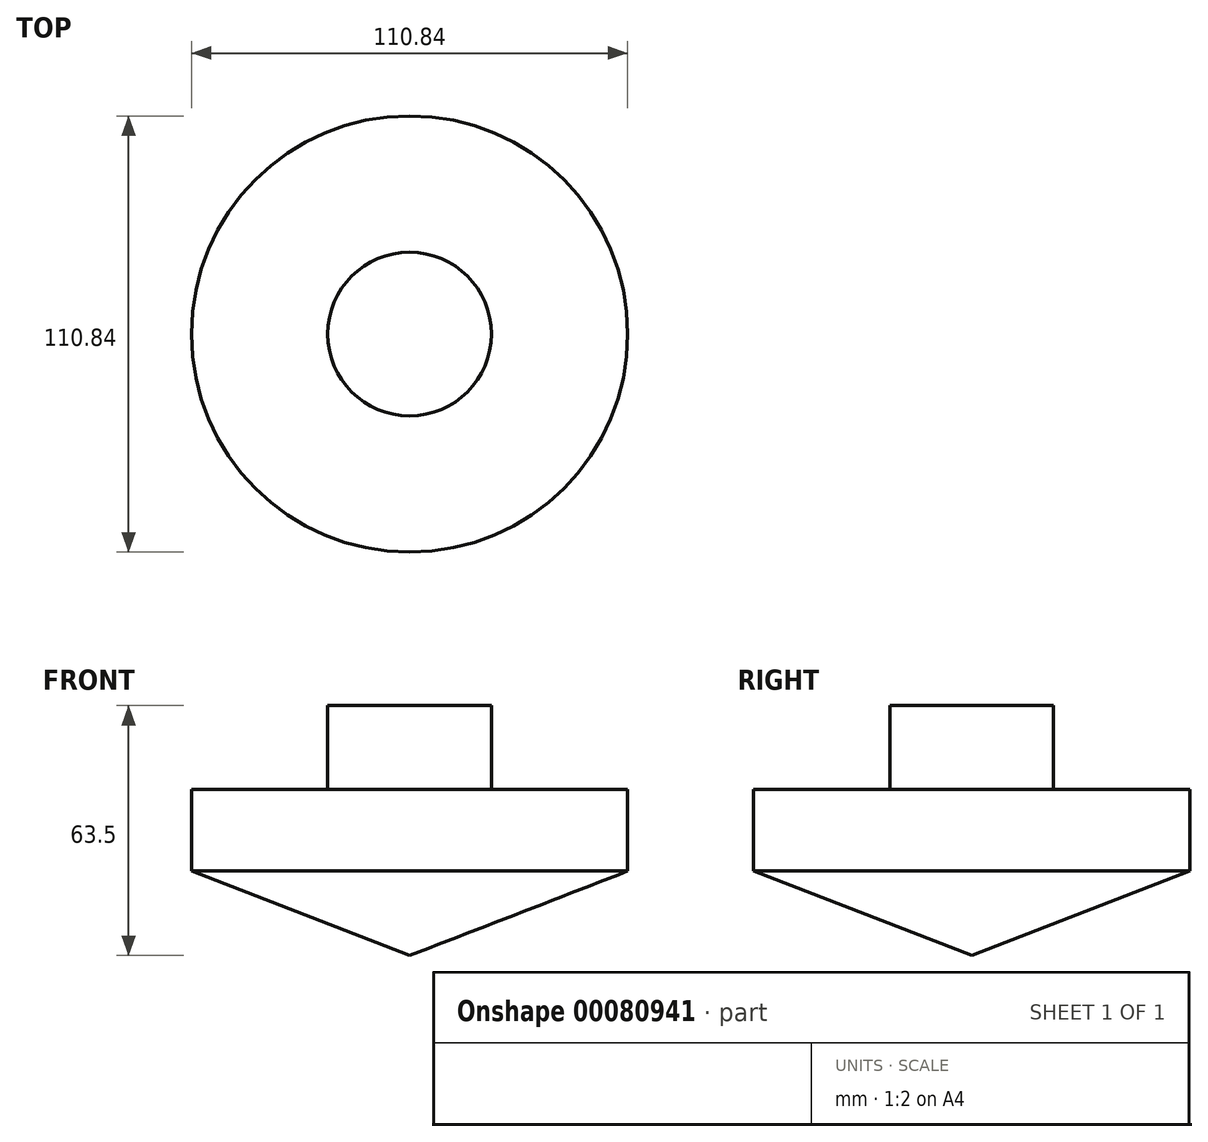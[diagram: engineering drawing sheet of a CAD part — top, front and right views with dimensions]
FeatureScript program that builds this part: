
annotation { "Feature Type Name" : "Feature", "Feature Type Description" : "" }
export const myFeature = defineFeature(function(context is Context, id is Id, definition is map)
    precondition{}
    {
        {
            var Q0;
            Q0=qCreatedBy(makeId("Front.planeOp"),FACE);
            var sketch = newSketch(context, id + "F0", { "sketchPlane" : qUnion([Q0])});
            skLineSegment(sketch, "E0", {"start": v(0, 0) * mm, "end": v(55.42, 21.47) * mm});
            skLineSegment(sketch, "E1", {"start": v(55.42, 21.47) * mm, "end": v(55.42, 42.26) * mm});
            skLineSegment(sketch, "E2", {"start": v(55.42, 42.26) * mm, "end": v(20.78, 42.26) * mm});
            skLineSegment(sketch, "E3", {"start": v(20.78, 42.26) * mm, "end": v(20.78, 63.5) * mm});
            skLineSegment(sketch, "E4", {"start": v(20.78, 63.5) * mm, "end": v(0, 63.5) * mm});
            skLineSegment(sketch, "E5", {"start": v(0, 63.5) * mm, "end": v(0, 0) * mm});
            skSolve(sketch);
        }
        {
            var Q0;
            Q0=makeQuery(id+"F0.imprint","IMPRINT",FACE,{"disambiguationData":[TD([[makeQuery(id+"F0.imprint","IMPRINT",EDGE,{"derivedFrom":sQuery(id+"F0.wireOp",EDGE,"E0")}),1.0]])]});
            var Q1;
            Q1=sQuery(id+"F0.wireOp",EDGE,"E5");
            revolve(context, id + "F1", {"entities" : qUnion([Q0]), "axis" : qUnion([Q1]), "revolveType" : RevolveType.FULL});
        }
    });
